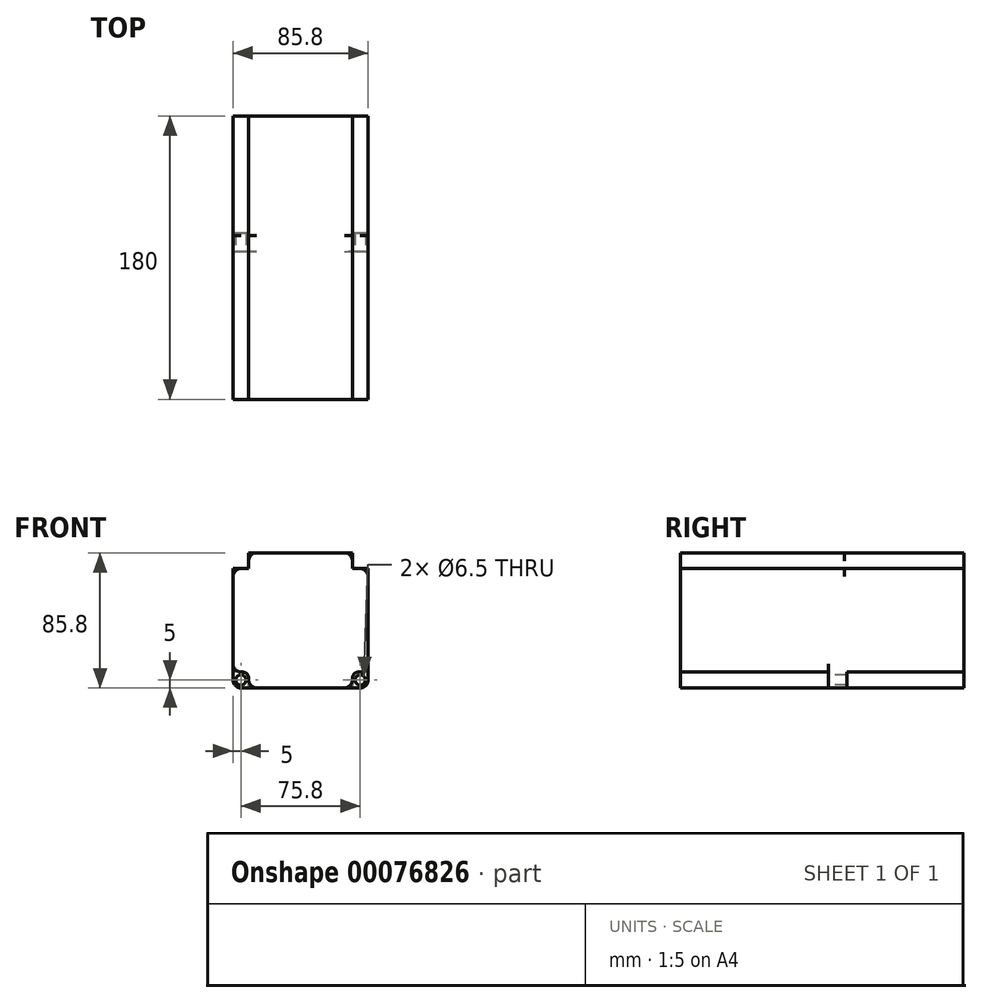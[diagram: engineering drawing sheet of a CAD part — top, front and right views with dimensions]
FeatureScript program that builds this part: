
annotation { "Feature Type Name" : "Feature", "Feature Type Description" : "" }
export const myFeature = defineFeature(function(context is Context, id is Id, definition is map)
    precondition{}
    {
        {
            var Q0;
            Q0=qCreatedBy(makeId("Front.planeOp"),FACE);
            var sketch = newSketch(context, id + "F0", { "sketchPlane" : qUnion([Q0])});
            skLineSegment(sketch, "E0.rect.bottom", {"start": v(42.9, -42.9) * mm, "end": v(-42.9, -42.9) * mm});
            skLineSegment(sketch, "E0.rect.top", {"start": v(42.9, 42.9) * mm, "end": v(-42.9, 42.9) * mm});
            skLineSegment(sketch, "E0.rect.left", {"start": v(42.9, -42.9) * mm, "end": v(42.9, 42.9) * mm});
            skLineSegment(sketch, "E0.rect.right", {"start": v(-42.9, -42.9) * mm, "end": v(-42.9, 42.9) * mm});
            skPoint(sketch, "E0.rect.middle", {"position": v(0, 0) * mm});
            skLineSegment(sketch, "E1.bottom", {"start": v(37.9, 42.9) * mm, "end": v(32.9, 42.9) * mm});
            skLineSegment(sketch, "E1.top", {"start": v(42.9, 32.9) * mm, "end": v(32.9, 32.9) * mm});
            skLineSegment(sketch, "E1.left", {"start": v(42.9, 37.9) * mm, "end": v(42.9, 32.9) * mm});
            skLineSegment(sketch, "E1.right", {"start": v(32.9, 42.9) * mm, "end": v(32.9, 32.9) * mm});
            skLineSegment(sketch, "E2.bottom", {"start": v(-37.9, 42.9) * mm, "end": v(-32.9, 42.9) * mm});
            skLineSegment(sketch, "E2.top", {"start": v(-42.9, 32.9) * mm, "end": v(-32.9, 32.9) * mm});
            skLineSegment(sketch, "E2.left", {"start": v(-42.9, 37.9) * mm, "end": v(-42.9, 32.9) * mm});
            skLineSegment(sketch, "E2.right", {"start": v(-32.9, 42.9) * mm, "end": v(-32.9, 32.9) * mm});
            skCircle(sketch, "E3", {"center": v(0, 0) * mm, "radius": 19.05 * mm});
            skCircle(sketch, "E4", {"center": v(0, 0) * mm, "radius": 7 * mm});
            skCircle(sketch, "E5", {"center": v(-37.9, 37.9) * mm, "radius": 3.25 * mm});
            skPoint(sketch, "E5.centerSnap0", {"position": v(-37.9, 42.9) * mm});
            skPoint(sketch, "E5.centerSnap1", {"position": v(-32.9, 37.9) * mm});
            skCircle(sketch, "E6", {"center": v(37.9, 37.9) * mm, "radius": 3.25 * mm});
            skPoint(sketch, "E6.centerSnap0", {"position": v(42.9, 37.9) * mm});
            skPoint(sketch, "E6.centerSnap1", {"position": v(37.9, 42.9) * mm});
            skPoint(sketch, "E7.visualSharp", {"position": v(-42.9, 42.9) * mm});
            skArc(sketch, "E7.filletArc", {"start": v(-37.9, 42.9) * mm, "mid": v(-41.44, 41.44) * mm, "end": v(-42.9, 37.9) * mm});
            skPoint(sketch, "E8.visualSharp", {"position": v(42.9, 42.9) * mm});
            skArc(sketch, "E8.filletArc", {"start": v(42.9, 37.9) * mm, "mid": v(41.44, 41.44) * mm, "end": v(37.9, 42.9) * mm});
            skPoint(sketch, "E9.visualSharp", {"position": v(42.9, -42.9) * mm});
            skPoint(sketch, "E10.visualSharp", {"position": v(-42.9, -42.9) * mm});
            skLineSegment(sketch, "E11", {"start": v(-42.9, -32.9) * mm, "end": v(-32.9, -32.9) * mm});
            skLineSegment(sketch, "E12", {"start": v(-32.9, -32.9) * mm, "end": v(-32.9, -42.9) * mm});
            skLineSegment(sketch, "E13", {"start": v(32.9, -42.9) * mm, "end": v(32.9, -32.9) * mm});
            skLineSegment(sketch, "E14", {"start": v(32.9, -32.9) * mm, "end": v(42.9, -32.9) * mm});
            skCircle(sketch, "E15", {"center": v(-37.9, -37.9) * mm, "radius": 3.25 * mm});
            skPoint(sketch, "E15.centerSnap0", {"position": v(-37.9, -32.9) * mm});
            skPoint(sketch, "E15.centerSnap1", {"position": v(-32.9, -37.9) * mm});
            skCircle(sketch, "E16", {"center": v(37.9, -37.9) * mm, "radius": 3.25 * mm});
            skPoint(sketch, "E16.centerSnap0", {"position": v(32.9, -37.9) * mm});
            skPoint(sketch, "E16.centerSnap1", {"position": v(37.9, -32.9) * mm});
            skArc(sketch, "E17", {"start": v(37.9, -42.9) * mm, "mid": v(41.43, -41.43) * mm, "end": v(42.9, -37.9) * mm});
            skArc(sketch, "E18", {"start": v(-42.9, -37.9) * mm, "mid": v(-41.43, -41.43) * mm, "end": v(-37.9, -42.9) * mm});
            skSolve(sketch);
        }
        {
            var Q0;
            {var subQ8=sQuery(id+"F0.wireOp",EDGE,"E1.top");Q0=makeQuery(id+"F0.imprint","IMPRINT",FACE,{"disambiguationData":[TD([[makeQuery(id+"F0.imprint","IMPRINT",EDGE,{"derivedFrom":subQ8}),1.0]])]});}
            var Q1;
            Q1=makeQuery(id+"F0.imprint","IMPRINT",FACE,{"disambiguationData":[TD([[makeQuery(id+"F0.imprint","IMPRINT",EDGE,{"derivedFrom":sQuery(id+"F0.wireOp",EDGE,"E2.bottom")}),-1.0]])]});
            var Q2;
            Q2=makeQuery(id+"F0.imprint","IMPRINT",FACE,{"disambiguationData":[TD([[makeQuery(id+"F0.imprint","IMPRINT",EDGE,{"derivedFrom":sQuery(id+"F0.wireOp",EDGE,"E1.bottom")}),1.0]])]});
            var Q3;
            Q3=makeQuery(id+"F0.imprint","IMPRINT",FACE,{"disambiguationData":[TD([[makeQuery(id+"F0.imprint","IMPRINT",EDGE,{"derivedFrom":sQuery(id+"F0.wireOp",EDGE,"E3")}),1.0]])]});
            var Q4;
            Q4=makeQuery(id+"F0.imprint","IMPRINT",FACE,{"disambiguationData":[TD([[makeQuery(id+"F0.imprint","IMPRINT",EDGE,{"derivedFrom":sQuery(id+"F0.wireOp",EDGE,"E4")}),1.0]])]});
            var Q5;
            {var subQ1=sQuery(id+"F0.wireOp",EDGE,"E11");Q5=makeQuery(id+"F0.imprint","IMPRINT",FACE,{"disambiguationData":[TD([[makeQuery(id+"F0.imprint","IMPRINT",EDGE,{"derivedFrom":subQ1}),-1.0]])]});}
            var Q6;
            {var subQ3=sQuery(id+"F0.wireOp",EDGE,"E13");Q6=makeQuery(id+"F0.imprint","IMPRINT",FACE,{"disambiguationData":[TD([[makeQuery(id+"F0.imprint","IMPRINT",EDGE,{"derivedFrom":subQ3}),-1.0]])]});}
            extrude(context, id + "F1", {"entities" : qUnion([Q0, Q1, Q2, Q3, Q4, Q5, Q6]), "oppositeDirection" : true, "depth" : 10 * mm});
        }
        {
            var Q0;
            Q0=makeQuery(id+"F1.opExtrude","CAP_FACE",FACE,{"disambiguationData":[OSD([sQuery(id+"F0.wireOp",EDGE,"E0.rect.bottom"),sQuery(id+"F0.wireOp",EDGE,"E0.rect.top"),sQuery(id+"F0.wireOp",EDGE,"E0.rect.left"),sQuery(id+"F0.wireOp",EDGE,"E0.rect.right"),sQuery(id+"F0.wireOp",EDGE,"E1.bottom"),sQuery(id+"F0.wireOp",EDGE,"E1.left"),sQuery(id+"F0.wireOp",EDGE,"E2.bottom"),sQuery(id+"F0.wireOp",EDGE,"E2.left"),sQuery(id+"F0.wireOp",EDGE,"E5"),sQuery(id+"F0.wireOp",EDGE,"E6"),sQuery(id+"F0.wireOp",EDGE,"E7.filletArc"),sQuery(id+"F0.wireOp",EDGE,"E8.filletArc"),sQuery(id+"F0.wireOp",EDGE,"E15"),sQuery(id+"F0.wireOp",EDGE,"E16"),sQuery(id+"F0.wireOp",EDGE,"E17"),sQuery(id+"F0.wireOp",EDGE,"E18")])],"isStart":false});
            var sketch = newSketch(context, id + "F2", { "sketchPlane" : qUnion([Q0])});
            skLineSegment(sketch, "E19.0", {"start": v(-32.9, 42.9) * mm, "end": v(-32.9, 36.7) * mm});
            skLineSegment(sketch, "E20.0", {"start": v(-42.9, 42.9) * mm, "end": v(42.9, 42.9) * mm});
            skLineSegment(sketch, "E21.0", {"start": v(-42.9, 32.9) * mm, "end": v(-36.7, 32.9) * mm});
            skLineSegment(sketch, "E22.0", {"start": v(32.9, 42.9) * mm, "end": v(32.9, 36.7) * mm});
            skLineSegment(sketch, "E23.0", {"start": v(42.9, 32.9) * mm, "end": v(36.7, 32.9) * mm});
            skLineSegment(sketch, "E24.0", {"start": v(42.9, -32.9) * mm, "end": v(36.7, -32.9) * mm});
            skLineSegment(sketch, "E25.0", {"start": v(32.9, -36.7) * mm, "end": v(32.9, -42.9) * mm});
            skLineSegment(sketch, "E26.0", {"start": v(-36.7, -32.9) * mm, "end": v(-42.9, -32.9) * mm});
            skLineSegment(sketch, "E27.0", {"start": v(-32.9, -42.9) * mm, "end": v(-32.9, -36.7) * mm});
            skPoint(sketch, "E28.visualSharp", {"position": v(-32.9, 32.9) * mm});
            skArc(sketch, "E28.filletArc", {"start": v(-36.7, 32.9) * mm, "mid": v(-34.02, 34.02) * mm, "end": v(-32.9, 36.7) * mm});
            skPoint(sketch, "E29.visualSharp", {"position": v(32.9, 32.9) * mm});
            skArc(sketch, "E29.filletArc", {"start": v(32.9, 36.7) * mm, "mid": v(34.02, 34.02) * mm, "end": v(36.7, 32.9) * mm});
            skPoint(sketch, "E30.visualSharp", {"position": v(32.9, -32.9) * mm});
            skArc(sketch, "E30.filletArc", {"start": v(36.7, -32.9) * mm, "mid": v(34.02, -34.02) * mm, "end": v(32.9, -36.7) * mm});
            skPoint(sketch, "E31.visualSharp", {"position": v(-32.9, -32.9) * mm});
            skArc(sketch, "E31.filletArc", {"start": v(-32.9, -36.7) * mm, "mid": v(-34.02, -34.02) * mm, "end": v(-36.7, -32.9) * mm});
            skSolve(sketch);
        }
        {
            var Q0;
            {var subQ5=sQuery(id+"F2.wireOp",EDGE,"E19.0");Q0=makeQuery(id+"F2.imprint","IMPRINT",FACE,{"disambiguationData":[TD([[makeQuery(id+"F2.imprint","IMPRINT",EDGE,{"derivedFrom":subQ5}),1.0]])]});}
            extrude(context, id + "F3", {"entities" : qUnion([Q0]), "operationType" : NewBodyOperationType.ADD, "oppositeDirection" : true, "depth" : 104 * mm});
        }
        {
            var Q0;
            Q0=makeQuery(id+"F3.opExtrude","SWEPT_EDGE",EDGE,{"disambiguationData":[OSD([sQuery(id+"F2.wireOp",EDGE,"E20.0"),sQuery(id+"F2.wireOp",EDGE,"E22.0")])]});
            var Q1;
            Q1=makeQuery(id+"F3.opExtrude","SWEPT_EDGE",EDGE,{"disambiguationData":[OSD([sQuery(id+"F2.wireOp",EDGE,"E19.0"),sQuery(id+"F2.wireOp",EDGE,"E20.0")])]});
            var Q2;
            Q2=makeQuery(id+"F3.opExtrude","SWEPT_EDGE",EDGE,{"disambiguationData":[OSD([sQuery(id+"F0.wireOp",EDGE,"E0.rect.left"),sQuery(id+"F0.wireOp",EDGE,"E1.left"),sQuery(id+"F2.wireOp",EDGE,"E21.0")])]});
            var Q3;
            Q3=makeQuery(id+"F3.opExtrude","SWEPT_EDGE",EDGE,{"disambiguationData":[OSD([sQuery(id+"F0.wireOp",EDGE,"E0.rect.right"),sQuery(id+"F0.wireOp",EDGE,"E2.left"),sQuery(id+"F2.wireOp",EDGE,"E23.0")])]});
            var Q4;
            Q4=makeQuery(id+"F3.opExtrude","SWEPT_EDGE",EDGE,{"disambiguationData":[OSD([sQuery(id+"F0.wireOp",EDGE,"E0.rect.right"),sQuery(id+"F0.wireOp",EDGE,"E2.left"),sQuery(id+"F2.wireOp",EDGE,"E24.0")])]});
            var Q5;
            Q5=makeQuery(id+"F3.opExtrude","SWEPT_EDGE",EDGE,{"disambiguationData":[OSD([sQuery(id+"F0.wireOp",EDGE,"E0.rect.bottom"),sQuery(id+"F2.wireOp",EDGE,"E25.0")])]});
            var Q6;
            Q6=makeQuery(id+"F3.opExtrude","SWEPT_EDGE",EDGE,{"disambiguationData":[OSD([sQuery(id+"F0.wireOp",EDGE,"E0.rect.bottom"),sQuery(id+"F2.wireOp",EDGE,"E27.0")])]});
            var Q7;
            Q7=makeQuery(id+"F3.opExtrude","SWEPT_EDGE",EDGE,{"disambiguationData":[OSD([sQuery(id+"F0.wireOp",EDGE,"E0.rect.left"),sQuery(id+"F0.wireOp",EDGE,"E1.left"),sQuery(id+"F2.wireOp",EDGE,"E26.0")])]});
            fillet(context, id + "F4", {"entities" : qUnion([Q0, Q1, Q2, Q3, Q4, Q5, Q6, Q7]), "radius" : 5.08 * mm, "tangentPropagation" : true, "allowEdgeOverflow" : false});
        }
        {
            var Q0;
            Q0=makeQuery(id+"F1.opExtrude","CAP_FACE",FACE,{"disambiguationData":[OSD([sQuery(id+"F0.wireOp",EDGE,"E0.rect.bottom"),sQuery(id+"F0.wireOp",EDGE,"E0.rect.top"),sQuery(id+"F0.wireOp",EDGE,"E0.rect.left"),sQuery(id+"F0.wireOp",EDGE,"E0.rect.right"),sQuery(id+"F0.wireOp",EDGE,"E1.bottom"),sQuery(id+"F0.wireOp",EDGE,"E1.left"),sQuery(id+"F0.wireOp",EDGE,"E2.bottom"),sQuery(id+"F0.wireOp",EDGE,"E2.left"),sQuery(id+"F0.wireOp",EDGE,"E5"),sQuery(id+"F0.wireOp",EDGE,"E6"),sQuery(id+"F0.wireOp",EDGE,"E7.filletArc"),sQuery(id+"F0.wireOp",EDGE,"E8.filletArc"),sQuery(id+"F0.wireOp",EDGE,"E15"),sQuery(id+"F0.wireOp",EDGE,"E16"),sQuery(id+"F0.wireOp",EDGE,"E17"),sQuery(id+"F0.wireOp",EDGE,"E18")])],"isStart":false});
            var sketch = newSketch(context, id + "F5", { "sketchPlane" : qUnion([Q0])});
            skCircle(sketch, "E32.0", {"center": v(0, 0) * mm, "radius": 7 * mm});
            skCircle(sketch, "E33.0", {"center": v(0, 0) * mm, "radius": 19.05 * mm});
            skSolve(sketch);
        }
        {
            var Q0;
            Q0=makeQuery(id+"F5.imprint","IMPRINT",FACE,{"disambiguationData":[TD([[makeQuery(id+"F5.imprint","IMPRINT",EDGE,{"derivedFrom":sQuery(id+"F5.wireOp",EDGE,"E32.0")}),-1.0]])]});
            extrude(context, id + "F6", {"entities" : qUnion([Q0]), "operationType" : NewBodyOperationType.ADD, "depth" : 34 * mm});
        }
        {
            var Q0;
            Q0=makeQuery(id+"F1.opExtrude","CAP_FACE",FACE,{"disambiguationData":[OSD([sQuery(id+"F0.wireOp",EDGE,"E0.rect.bottom"),sQuery(id+"F0.wireOp",EDGE,"E0.rect.top"),sQuery(id+"F0.wireOp",EDGE,"E0.rect.left"),sQuery(id+"F0.wireOp",EDGE,"E0.rect.right"),sQuery(id+"F0.wireOp",EDGE,"E1.bottom"),sQuery(id+"F0.wireOp",EDGE,"E1.left"),sQuery(id+"F0.wireOp",EDGE,"E2.bottom"),sQuery(id+"F0.wireOp",EDGE,"E2.left"),sQuery(id+"F0.wireOp",EDGE,"E5"),sQuery(id+"F0.wireOp",EDGE,"E6"),sQuery(id+"F0.wireOp",EDGE,"E7.filletArc"),sQuery(id+"F0.wireOp",EDGE,"E8.filletArc"),sQuery(id+"F0.wireOp",EDGE,"E15"),sQuery(id+"F0.wireOp",EDGE,"E16"),sQuery(id+"F0.wireOp",EDGE,"E17"),sQuery(id+"F0.wireOp",EDGE,"E18")])],"isStart":false});
            var sketch = newSketch(context, id + "F7", { "sketchPlane" : qUnion([Q0])});
            skCircle(sketch, "E34.0", {"center": v(0, 0) * mm, "radius": 19.05 * mm});
            skSolve(sketch);
        }
        {
            var Q0;
            Q0=makeQuery(id+"F7.imprint","IMPRINT",FACE,{"disambiguationData":[TD([[makeQuery(id+"F7.imprint","IMPRINT",EDGE,{"derivedFrom":sQuery(id+"F7.wireOp",EDGE,"E34.0")}),-1.0]])]});
            extrude(context, id + "F8", {"entities" : qUnion([Q0]), "operationType" : NewBodyOperationType.ADD, "depth" : 1.6 * mm});
        }
        {
            var Q0;
            {var subQ5=sQuery(id+"F2.wireOp",EDGE,"E19.0");Q0=makeQuery(id+"F2.imprint","IMPRINT",FACE,{"disambiguationData":[TD([[makeQuery(id+"F2.imprint","IMPRINT",EDGE,{"derivedFrom":subQ5}),1.0]])]});}
            extrude(context, id + "F9", {"entities" : qUnion([Q0]), "operationType" : NewBodyOperationType.ADD, "depth" : 76 * mm});
        }
    });
